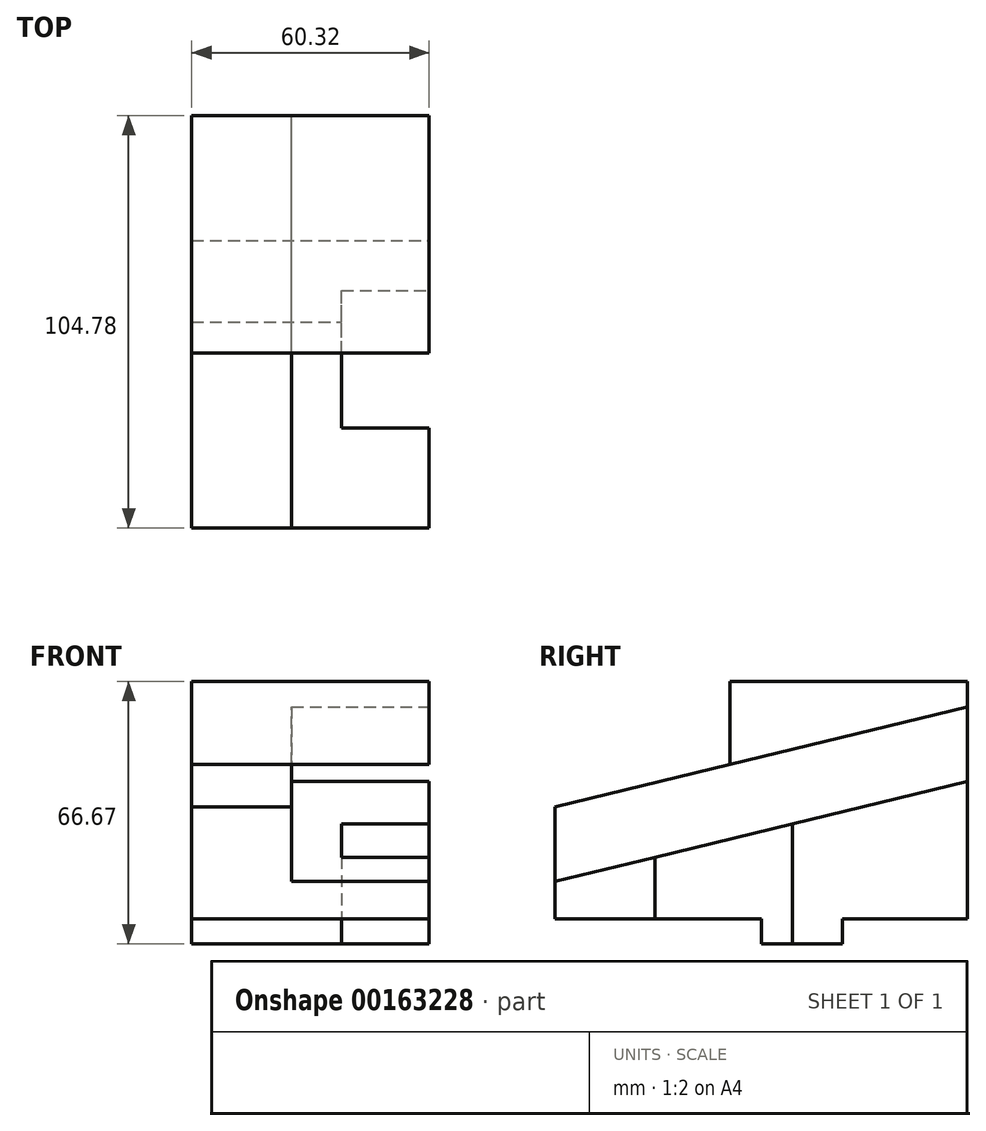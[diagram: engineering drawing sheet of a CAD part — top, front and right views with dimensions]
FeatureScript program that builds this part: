
annotation { "Feature Type Name" : "Feature", "Feature Type Description" : "" }
export const myFeature = defineFeature(function(context is Context, id is Id, definition is map)
    precondition{}
    {
        {
            var Q0;
            Q0=qCreatedBy(makeId("Top.planeOp"),FACE);
            var sketch = newSketch(context, id + "F0", { "sketchPlane" : qUnion([Q0])});
            skLineSegment(sketch, "E0.bottom", {"start": v(30.16, -52.39) * mm, "end": v(-30.16, -52.39) * mm});
            skLineSegment(sketch, "E0.top", {"start": v(30.16, 52.39) * mm, "end": v(-30.16, 52.39) * mm});
            skLineSegment(sketch, "E0.left", {"start": v(30.16, -52.39) * mm, "end": v(30.16, 52.39) * mm});
            skLineSegment(sketch, "E0.right", {"start": v(-30.16, -52.39) * mm, "end": v(-30.16, 52.39) * mm});
            skPoint(sketch, "E0.middle", {"position": v(0, 0) * mm});
            skSolve(sketch);
        }
        {
            var Q0;
            Q0=makeQuery(id+"F0.imprint","IMPRINT",FACE,{"disambiguationData":[TD([[makeQuery(id+"F0.imprint","IMPRINT",EDGE,{"derivedFrom":sQuery(id+"F0.wireOp",EDGE,"E0.bottom")}),-1.0]])]});
            extrude(context, id + "F1", {"entities" : qUnion([Q0]), "depth" : 66.67 * mm});
        }
        {
            var Q0;
            Q0=makeQuery(id+"F1.opExtrude","SWEPT_FACE",FACE,{"disambiguationData":[OSD([sQuery(id+"F0.wireOp",EDGE,"E0.left")])]});
            var sketch = newSketch(context, id + "F2", { "sketchPlane" : qUnion([Q0])});
            skLineSegment(sketch, "E1", {"start": v(-52.39, 15.87) * mm, "end": v(52.39, 41.28) * mm});
            skLineSegment(sketch, "E2.0", {"start": v(-52.39, 34.82) * mm, "end": v(52.39, 60.22) * mm});
            skLineSegment(sketch, "E3", {"start": v(-52.39, 34.82) * mm, "end": v(-52.39, 15.87) * mm});
            skLineSegment(sketch, "E4", {"start": v(52.39, 60.22) * mm, "end": v(52.39, 41.28) * mm});
            skSolve(sketch);
        }
        {
            var Q0;
            Q0=makeQuery(id+"F2.imprint","IMPRINT",FACE,{"disambiguationData":[TD([[makeQuery(id+"F2.imprint","IMPRINT",EDGE,{"derivedFrom":sQuery(id+"F2.wireOp",EDGE,"E1")}),1.0]])]});
            extrude(context, id + "F3", {"entities" : qUnion([Q0]), "operationType" : NewBodyOperationType.REMOVE, "oppositeDirection" : true, "depth" : 34.92 * mm});
        }
        {
            var Q0;
            {var subQ1=sQuery(id+"F0.wireOp",EDGE,"E0.left");Q0=makeQuery(id+"F3.boolean.opBoolean","SPLIT",FACE,{"disambiguationData":[TD([makeQuery(id+"F3.opExtrude","SWEPT_FACE",FACE,{"disambiguationData":[OSD([sQuery(id+"F2.wireOp",EDGE,"E1")])]})])],"derivedFrom":makeQuery(id+"F1.opExtrude","SWEPT_FACE",FACE,{"disambiguationData":[OSD([subQ1])]})});}
            var sketch = newSketch(context, id + "F4", { "sketchPlane" : qUnion([Q0])});
            skLineSegment(sketch, "E5.bottom", {"start": v(-26.99, 30.5) * mm, "end": v(7.94, 30.5) * mm});
            skLineSegment(sketch, "E5.top", {"start": v(-26.99, 0) * mm, "end": v(7.94, 0) * mm});
            skLineSegment(sketch, "E5.left", {"start": v(-26.99, 30.5) * mm, "end": v(-26.99, 0) * mm});
            skLineSegment(sketch, "E5.right", {"start": v(7.94, 30.5) * mm, "end": v(7.94, 0) * mm});
            skSolve(sketch);
        }
        {
            var Q0;
            {var subQ0=sQuery(id+"F4.wireOp",EDGE,"E5.top");Q0=makeQuery(id+"F4.imprint","IMPRINT",FACE,{"disambiguationData":[TD([[makeQuery(id+"F4.imprint","IMPRINT",EDGE,{"derivedFrom":subQ0}),1.0]])]});}
            extrude(context, id + "F5", {"entities" : qUnion([Q0]), "operationType" : NewBodyOperationType.REMOVE, "oppositeDirection" : true, "depth" : 22.22 * mm});
        }
        {
            var Q0;
            {var subQ0=sQuery(id+"F0.wireOp",EDGE,"E0.bottom");var subQ1=makeQuery(id+"F1.opExtrude","SWEPT_FACE",FACE,{"disambiguationData":[OSD([subQ0])]});var subQ2=sQuery(id+"F0.wireOp",EDGE,"E0.left");var subQ5=makeQuery(id+"F3.opExtrude","SWEPT_FACE",FACE,{"disambiguationData":[OSD([sQuery(id+"F2.wireOp",EDGE,"E1")])]});Q0=makeQuery(id+"F5.boolean.opBoolean","SPLIT",FACE,{"disambiguationData":[TD([subQ1])],"derivedFrom":makeQuery(id+"F3.boolean.opBoolean","SPLIT",FACE,{"disambiguationData":[TD([subQ5])],"derivedFrom":makeQuery(id+"F1.opExtrude","SWEPT_FACE",FACE,{"disambiguationData":[OSD([subQ2])]})})});}
            var sketch = newSketch(context, id + "F6", { "sketchPlane" : qUnion([Q0])});
            skLineSegment(sketch, "E6", {"start": v(-52.39, 6.35) * mm, "end": v(0, 6.35) * mm});
            skLineSegment(sketch, "E7", {"start": v(0, 6.35) * mm, "end": v(0, 0) * mm});
            skLineSegment(sketch, "E8", {"start": v(52.5, 6.35) * mm, "end": v(20.64, 6.35) * mm});
            skLineSegment(sketch, "E9", {"start": v(20.64, 6.35) * mm, "end": v(20.64, 0) * mm});
            skLineSegment(sketch, "E10", {"start": v(-52.39, 6.35) * mm, "end": v(-52.39, 0) * mm});
            skLineSegment(sketch, "E11", {"start": v(-52.39, 0) * mm, "end": v(0, 0) * mm});
            skLineSegment(sketch, "E12", {"start": v(20.64, 0) * mm, "end": v(52.8, 0) * mm});
            skLineSegment(sketch, "E13", {"start": v(52.8, 0) * mm, "end": v(52.5, 6.35) * mm});
            skSolve(sketch);
        }
        {
            var Q0;
            {var subQ0=sQuery(id+"F6.wireOp",EDGE,"E7");Q0=makeQuery(id+"F6.imprint","IMPRINT",FACE,{"disambiguationData":[TD([[makeQuery(id+"F6.imprint","IMPRINT",EDGE,{"derivedFrom":subQ0}),-1.0]])]});}
            var Q1;
            {var subQ0=sQuery(id+"F6.wireOp",EDGE,"E10");Q1=makeQuery(id+"F6.imprint","IMPRINT",FACE,{"disambiguationData":[TD([[makeQuery(id+"F6.imprint","IMPRINT",EDGE,{"derivedFrom":subQ0}),1.0]])]});}
            var Q2;
            Q2=makeQuery(id+"F6.imprint","IMPRINT",FACE,{"disambiguationData":[TD([[makeQuery(id+"F6.imprint","IMPRINT",EDGE,{"derivedFrom":sQuery(id+"F6.wireOp",EDGE,"E8")}),1.0]])]});
            extrude(context, id + "F7", {"entities" : qUnion([Q0, Q1, Q2]), "operationType" : NewBodyOperationType.REMOVE, "endBound" : BoundingType.THROUGH_ALL, "oppositeDirection" : true, "depth" : 25.4 * mm});
        }
        {
            var Q0;
            {var subQ1=sQuery(id+"F0.wireOp",EDGE,"E0.left");Q0=makeQuery(id+"F3.boolean.opBoolean","SPLIT",FACE,{"disambiguationData":[TD([makeQuery(id+"F3.opExtrude","SWEPT_FACE",FACE,{"disambiguationData":[OSD([sQuery(id+"F2.wireOp",EDGE,"E2.0")])]})])],"derivedFrom":makeQuery(id+"F1.opExtrude","SWEPT_FACE",FACE,{"disambiguationData":[OSD([subQ1])]})});}
            var sketch = newSketch(context, id + "F8", { "sketchPlane" : qUnion([Q0])});
            skLineSegment(sketch, "E14", {"start": v(-7.94, 66.68) * mm, "end": v(-7.94, 45.6) * mm});
            skLineSegment(sketch, "E15", {"start": v(-7.94, 45.6) * mm, "end": v(-52.39, 34.82) * mm});
            skLineSegment(sketch, "E16", {"start": v(-52.39, 34.82) * mm, "end": v(-52.39, 66.68) * mm});
            skLineSegment(sketch, "E17", {"start": v(-52.39, 66.68) * mm, "end": v(-7.94, 66.68) * mm});
            skLineSegment(sketch, "E18.0", {"start": v(52.39, 66.68) * mm, "end": v(52.39, 60.22) * mm, "construction": true});
            skSolve(sketch);
        }
        {
            var Q0;
            Q0=makeQuery(id+"F8.imprint","IMPRINT",FACE,{"disambiguationData":[TD([[makeQuery(id+"F8.imprint","IMPRINT",EDGE,{"derivedFrom":sQuery(id+"F8.wireOp",EDGE,"E14")}),-1.0]])]});
            extrude(context, id + "F9", {"entities" : qUnion([Q0]), "operationType" : NewBodyOperationType.REMOVE, "endBound" : BoundingType.THROUGH_ALL, "oppositeDirection" : true, "depth" : 25.4 * mm});
        }
    });
